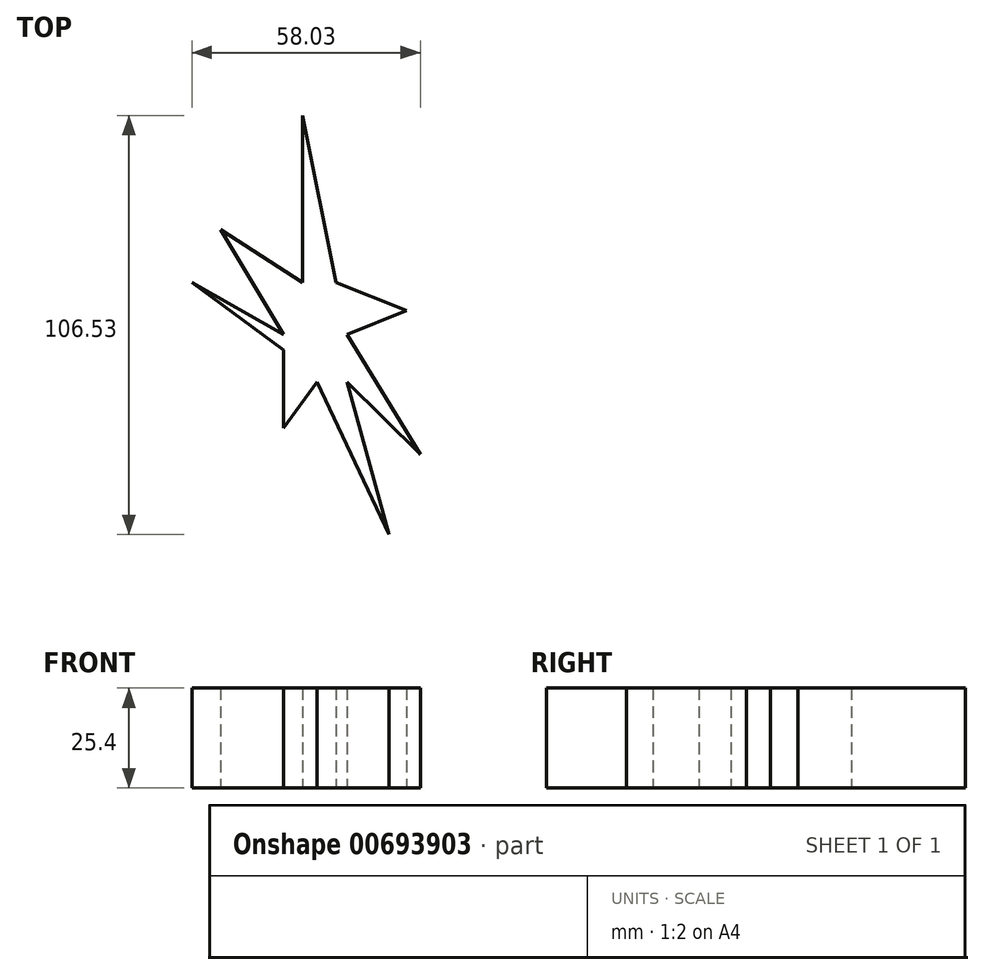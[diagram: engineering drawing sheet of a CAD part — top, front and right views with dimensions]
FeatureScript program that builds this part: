
annotation { "Feature Type Name" : "Feature", "Feature Type Description" : "" }
export const myFeature = defineFeature(function(context is Context, id is Id, definition is map)
    precondition{}
    {
        {
            var Q0;
            Q0=qCreatedBy(makeId("Top.planeOp"),FACE);
            var sketch = newSketch(context, id + "F0", { "sketchPlane" : qUnion([Q0])});
            skLineSegment(sketch, "E0", {"start": v(0, 0) * mm, "end": v(0, 42.53) * mm});
            skLineSegment(sketch, "E1", {"start": v(0, 42.53) * mm, "end": v(8.62, 0) * mm});
            skLineSegment(sketch, "E2", {"start": v(8.62, 0) * mm, "end": v(26.5, -7) * mm});
            skLineSegment(sketch, "E3", {"start": v(26.5, -7) * mm, "end": v(11.35, -13.12) * mm});
            skLineSegment(sketch, "E4", {"start": v(11.35, -13.12) * mm, "end": v(29.97, -43.68) * mm});
            skLineSegment(sketch, "E5", {"start": v(29.97, -43.68) * mm, "end": v(11.35, -25.25) * mm});
            skLineSegment(sketch, "E6", {"start": v(11.35, -25.25) * mm, "end": v(22.03, -64) * mm});
            skLineSegment(sketch, "E7", {"start": v(22.03, -64) * mm, "end": v(3.73, -25.25) * mm});
            skLineSegment(sketch, "E8", {"start": v(3.73, -25.25) * mm, "end": v(-4.78, -36.86) * mm});
            skLineSegment(sketch, "E9", {"start": v(-4.78, -36.86) * mm, "end": v(-4.78, -17.06) * mm});
            skLineSegment(sketch, "E10", {"start": v(-4.78, -17.06) * mm, "end": v(-28.06, 0) * mm});
            skLineSegment(sketch, "E11", {"start": v(-28.06, 0) * mm, "end": v(-4.78, -13.12) * mm});
            skLineSegment(sketch, "E12", {"start": v(-4.78, -13.12) * mm, "end": v(-20.79, 13.57) * mm});
            skLineSegment(sketch, "E13", {"start": v(-20.79, 13.57) * mm, "end": v(0, 0) * mm});
            skSolve(sketch);
        }
        {
            var Q0;
            Q0=makeQuery(id+"F0.imprint","IMPRINT",FACE,{"disambiguationData":[TD([[makeQuery(id+"F0.imprint","IMPRINT",EDGE,{"derivedFrom":sQuery(id+"F0.wireOp",EDGE,"E0")}),-1.0]])]});
            extrude(context, id + "F1", {"entities" : qUnion([Q0]), "depth" : 25.4 * mm, "offsetDistance" : 25.4 * mm});
        }
    });
